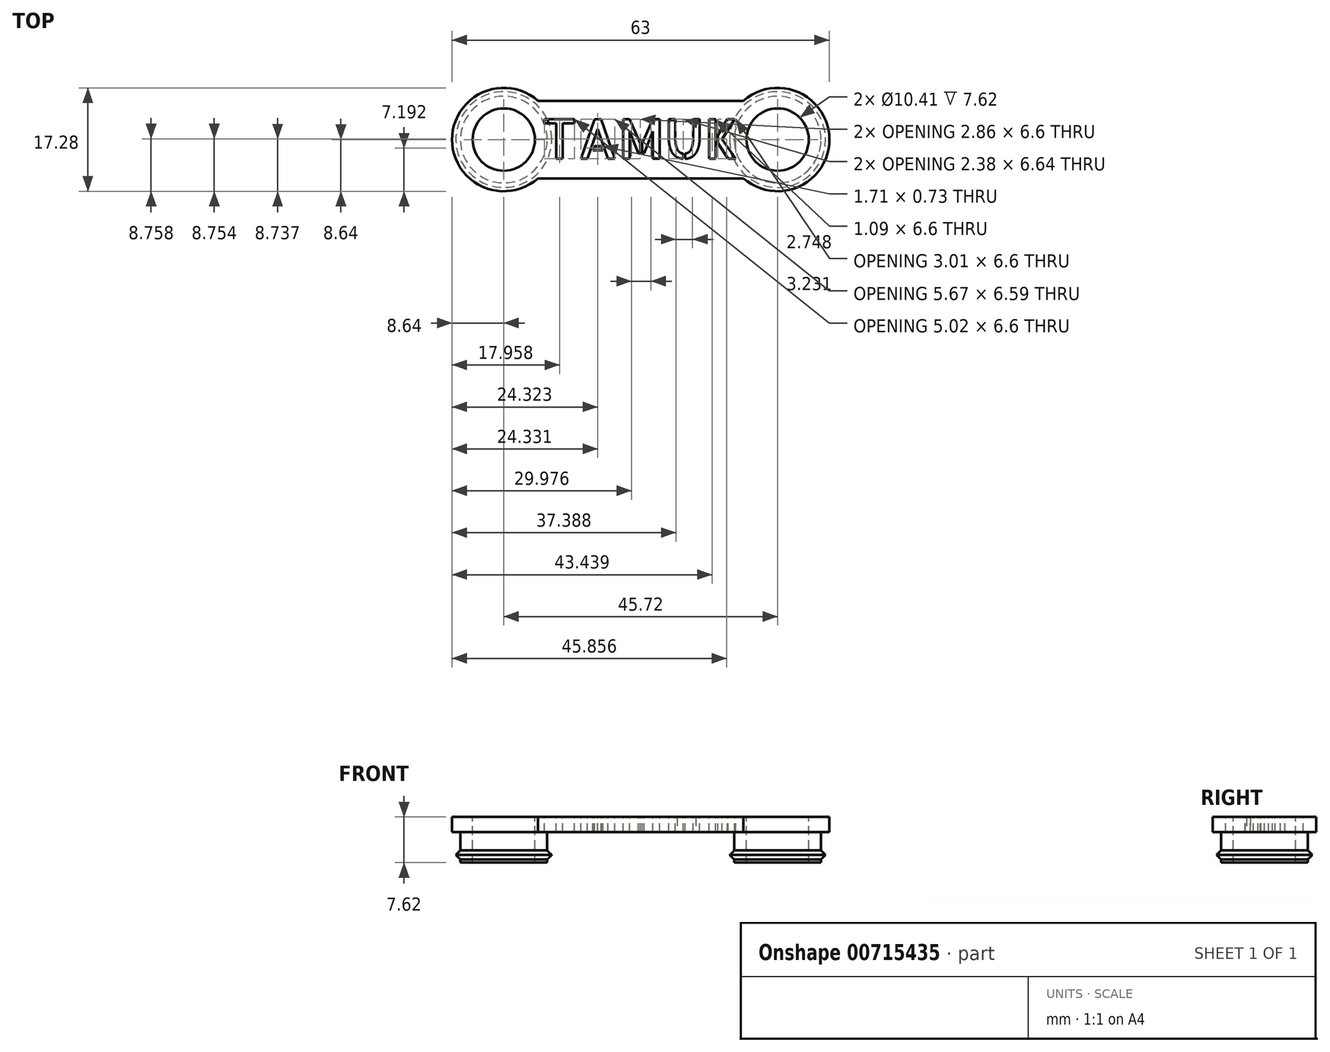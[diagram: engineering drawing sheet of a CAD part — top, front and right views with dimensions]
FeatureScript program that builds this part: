
annotation { "Feature Type Name" : "Feature", "Feature Type Description" : "" }
export const myFeature = defineFeature(function(context is Context, id is Id, definition is map)
    precondition{}
    {
        {
            var Q0;
            Q0=qCreatedBy(makeId("Top.planeOp"),FACE);
            var sketch = newSketch(context, id + "F0", { "sketchPlane" : qUnion([Q0])});
            skLineSegment(sketch, "E0", {"start": v(-17.15, -6.48) * mm, "end": v(17.15, -6.48) * mm});
            skLineSegment(sketch, "E1", {"start": v(-17.15, 6.48) * mm, "end": v(17.15, 6.48) * mm});
            skPoint(sketch, "E2", {"position": v(0, 6.48) * mm});
            skArc(sketch, "E3", {"start": v(-17.15, 6.48) * mm, "mid": v(-31.5, 0) * mm, "end": v(-17.15, -6.48) * mm});
            skArc(sketch, "E4", {"start": v(17.15, -6.48) * mm, "mid": v(31.5, 0) * mm, "end": v(17.15, 6.48) * mm});
            skSolve(sketch);
        }
        {
            var Q0;
            Q0=qCreatedBy(makeId("Front.planeOp"),FACE);
            var sketch = newSketch(context, id + "F1", { "sketchPlane" : qUnion([Q0])});
            skLineSegment(sketch, "E5", {"start": v(-28.07, 7.11) * mm, "end": v(-30.1, 7.11) * mm});
            skLineSegment(sketch, "E6", {"start": v(-30.1, 7.11) * mm, "end": v(-30.1, 6.6) * mm});
            skLineSegment(sketch, "E7", {"start": v(-30.1, 6.6) * mm, "end": v(-30.86, 5.84) * mm});
            skLineSegment(sketch, "E8", {"start": v(-30.86, 5.84) * mm, "end": v(-30.1, 5.08) * mm});
            skLineSegment(sketch, "E9", {"start": v(-22.86, 2.03) * mm, "end": v(-22.86, 0) * mm});
            skLineSegment(sketch, "E10", {"start": v(-28.07, 7.11) * mm, "end": v(-28.07, 2.03) * mm});
            skLineSegment(sketch, "E11", {"start": v(-30.1, 5.08) * mm, "end": v(-30.1, 2.03) * mm});
            skLineSegment(sketch, "E12", {"start": v(-28.07, 2.03) * mm, "end": v(-30.1, 2.03) * mm});
            skLineSegment(sketch, "E13", {"start": v(-22.86, 2.03) * mm, "end": v(-30.1, 2.03) * mm});
            skLineSegment(sketch, "E14.MirrorCS", {"start": v(-30.1, -6.6) * mm, "end": v(-30.86, -5.84) * mm});
            skLineSegment(sketch, "E15.MirrorCS", {"start": v(-30.1, -7.11) * mm, "end": v(-30.1, -6.6) * mm});
            skLineSegment(sketch, "E16.MirrorCS", {"start": v(-28.07, -7.11) * mm, "end": v(-30.1, -7.11) * mm});
            skLineSegment(sketch, "E17.MirrorCS", {"start": v(-28.07, -7.11) * mm, "end": v(-28.07, -2.03) * mm});
            skLineSegment(sketch, "E18.MirrorCS", {"start": v(-30.1, -5.08) * mm, "end": v(-30.1, -2.03) * mm});
            skLineSegment(sketch, "E19.MirrorCS", {"start": v(-22.86, -2.03) * mm, "end": v(-30.1, -2.03) * mm});
            skLineSegment(sketch, "E20.MirrorCS", {"start": v(-30.86, -5.84) * mm, "end": v(-30.1, -5.08) * mm});
            skSolve(sketch);
        }
        {
            var Q0;
            Q0=makeQuery(id+"F0.imprint","IMPRINT",FACE,{"disambiguationData":[TD([[makeQuery(id+"F0.imprint","IMPRINT",EDGE,{"derivedFrom":sQuery(id+"F0.wireOp",EDGE,"E0")}),1.0]])]});
            extrude(context, id + "F2", {"entities" : qUnion([Q0]), "oppositeDirection" : true, "depth" : 2.03 * mm, "offsetDistance" : 25.4 * mm});
        }
        {
            var Q0;
            Q0=makeQuery(id+"F1.imprint","IMPRINT",FACE,{"disambiguationData":[TD([[makeQuery(id+"F1.imprint","IMPRINT",EDGE,{"derivedFrom":sQuery(id+"F1.wireOp",EDGE,"E14.MirrorCS")}),-1.0]])]});
            var Q1;
            Q1=sQuery(id+"F1.wireOp",EDGE,"E9");
            revolve(context, id + "F3", {"operationType" : NewBodyOperationType.ADD, "surfaceOperationType" : NewSurfaceOperationType.NEW, "entities" : qUnion([Q0]), "axis" : qUnion([Q1]), "revolveType" : RevolveType.FULL});
        }
        {
            var Q0;
            Q0=makeQuery(id+"F2.opExtrude","SWEPT_BODY",BODY,{"disambiguationData":[OSD([sQuery(id+"F0.wireOp",EDGE,"E0"),sQuery(id+"F0.wireOp",EDGE,"E1"),sQuery(id+"F0.wireOp",EDGE,"E3"),sQuery(id+"F0.wireOp",EDGE,"E4")])]});
            var Q1;
            Q1=qCreatedBy(makeId("Right.planeOp"),FACE);
            mirror(context, id + "F4", {"operationType" : NewBodyOperationType.ADD, "entities" : qUnion([Q0]), "mirrorPlane" : qUnion([Q1])});
        }
        {
            var Q0;
            {var subQ0=sQuery(id+"F0.wireOp",EDGE,"E3");var subQ1=sQuery(id+"F0.wireOp",EDGE,"E1");var subQ2=sQuery(id+"F0.wireOp",EDGE,"E4");var subQ3=sQuery(id+"F0.wireOp",EDGE,"E0");Q0=makeQuery(id+"F4.boolean.opBoolean","SPLIT",FACE,{"disambiguationData":[TD([makeQuery(id+"F4.opPattern","COPY",FACE,{"derivedFrom":makeQuery(id+"F3.opRevolve","SWEPT_FACE",FACE,{"disambiguationData":[OSD([sQuery(id+"F1.wireOp",EDGE,"E17.MirrorCS")])]}),"instanceName":"1"})])],"derivedFrom":makeQuery(id+"F3.boolean.opBoolean","SPLIT",FACE,{"disambiguationData":[TD([makeQuery(id+"F2.opExtrude","SWEPT_FACE",FACE,{"disambiguationData":[OSD([subQ3])]})])],"derivedFrom":makeQuery(id+"F2.opExtrude","CAP_FACE",FACE,{"disambiguationData":[OSD([subQ3,subQ1,subQ0,subQ2])],"isStart":false})})});}
            var Q1;
            Q1=makeQuery(id+"F3.boolean.opBoolean","SPLIT",FACE,{"disambiguationData":[TD([makeQuery(id+"F3.opRevolve","SWEPT_FACE",FACE,{"disambiguationData":[OSD([sQuery(id+"F1.wireOp",EDGE,"E17.MirrorCS")])]})])],"derivedFrom":makeQuery(id+"F2.opExtrude","CAP_FACE",FACE,{"disambiguationData":[OSD([sQuery(id+"F0.wireOp",EDGE,"E0"),sQuery(id+"F0.wireOp",EDGE,"E1"),sQuery(id+"F0.wireOp",EDGE,"E3"),sQuery(id+"F0.wireOp",EDGE,"E4")])],"isStart":false})});
            extrude(context, id + "F5", {"entities" : qUnion([Q0, Q1]), "operationType" : NewBodyOperationType.REMOVE, "oppositeDirection" : true, "depth" : 25.4 * mm, "offsetDistance" : 25.4 * mm});
        }
        {
            var Q0;
            Q0=makeQuery(id+"F2.opExtrude","CAP_FACE",FACE,{"disambiguationData":[OSD([sQuery(id+"F0.wireOp",EDGE,"E0"),sQuery(id+"F0.wireOp",EDGE,"E1"),sQuery(id+"F0.wireOp",EDGE,"E3"),sQuery(id+"F0.wireOp",EDGE,"E4")])],"isStart":true});
            extrude(context, id + "F6", {"entities" : qUnion([Q0]), "operationType" : NewBodyOperationType.ADD, "depth" : 0.5 * mm, "offsetDistance" : 25.4 * mm});
        }
        {
            var Q0;
            Q0=makeQuery(id+"F6.opExtrude","CAP_FACE",FACE,{"disambiguationData":[OSD([sQuery(id+"F0.wireOp",EDGE,"E0"),sQuery(id+"F0.wireOp",EDGE,"E1"),sQuery(id+"F0.wireOp",EDGE,"E3"),sQuery(id+"F0.wireOp",EDGE,"E4")])],"isStart":false});
            var sketch = newSketch(context, id + "F7", { "sketchPlane" : qUnion([Q0])});
            skText(sketch, "E21", { "text": "TAMUK", "fontName": "AllertaStencil-Regular.ttf"});
            const initialGuessF7  = {"E21": [-0.01651, -0.00318, 1, 0, 0.0066]};
            skSetInitialGuess(sketch, initialGuessF7);
            skSolve(sketch);
        }
        {
            var Q0;
            Q0=makeQuery(id+"F7.imprint","IMPRINT",FACE,{"disambiguationData":[TD([[makeQuery(id+"F7.imprint","IMPRINT",EDGE,{"derivedFrom":sQuery(id+"F7.wireOp",EDGE,"E21.sketch_text.stroke-0")}),-1.0]])]});
            var Q1;
            Q1=makeQuery(id+"F7.imprint","IMPRINT",FACE,{"disambiguationData":[TD([[makeQuery(id+"F7.imprint","IMPRINT",EDGE,{"derivedFrom":sQuery(id+"F7.wireOp",EDGE,"E21.sketch_text.stroke-8")}),-1.0]])]});
            var Q2;
            Q2=makeQuery(id+"F7.imprint","IMPRINT",FACE,{"disambiguationData":[TD([[makeQuery(id+"F7.imprint","IMPRINT",EDGE,{"derivedFrom":sQuery(id+"F7.wireOp",EDGE,"E21.sketch_text.stroke-15")}),-1.0]])]});
            var Q3;
            Q3=makeQuery(id+"F7.imprint","IMPRINT",FACE,{"disambiguationData":[TD([[makeQuery(id+"F7.imprint","IMPRINT",EDGE,{"derivedFrom":sQuery(id+"F7.wireOp",EDGE,"E21.sketch_text.stroke-19")}),-1.0]])]});
            var Q4;
            Q4=makeQuery(id+"F7.imprint","IMPRINT",FACE,{"disambiguationData":[TD([[makeQuery(id+"F7.imprint","IMPRINT",EDGE,{"derivedFrom":sQuery(id+"F7.wireOp",EDGE,"E21.sketch_text.stroke-27")}),-1.0]])]});
            var Q5;
            Q5=makeQuery(id+"F7.imprint","IMPRINT",FACE,{"disambiguationData":[TD([[makeQuery(id+"F7.imprint","IMPRINT",EDGE,{"derivedFrom":sQuery(id+"F7.wireOp",EDGE,"E21.sketch_text.stroke-35")}),-1.0]])]});
            var Q6;
            Q6=makeQuery(id+"F7.imprint","IMPRINT",FACE,{"disambiguationData":[TD([[makeQuery(id+"F7.imprint","IMPRINT",EDGE,{"derivedFrom":sQuery(id+"F7.wireOp",EDGE,"E21.sketch_text.stroke-47")}),-1.0]])]});
            var Q7;
            Q7=makeQuery(id+"F7.imprint","IMPRINT",FACE,{"disambiguationData":[TD([[makeQuery(id+"F7.imprint","IMPRINT",EDGE,{"derivedFrom":sQuery(id+"F7.wireOp",EDGE,"E21.sketch_text.stroke-59")}),-1.0]])]});
            var Q8;
            Q8=makeQuery(id+"F7.imprint","IMPRINT",FACE,{"disambiguationData":[TD([[makeQuery(id+"F7.imprint","IMPRINT",EDGE,{"derivedFrom":sQuery(id+"F7.wireOp",EDGE,"E21.sketch_text.stroke-63")}),-1.0]])]});
            extrude(context, id + "F8", {"entities" : qUnion([Q0, Q1, Q2, Q3, Q4, Q5, Q6, Q7, Q8]), "operationType" : NewBodyOperationType.REMOVE, "oppositeDirection" : true, "depth" : 2.54 * mm, "offsetDistance" : 25.4 * mm});
        }
    });
